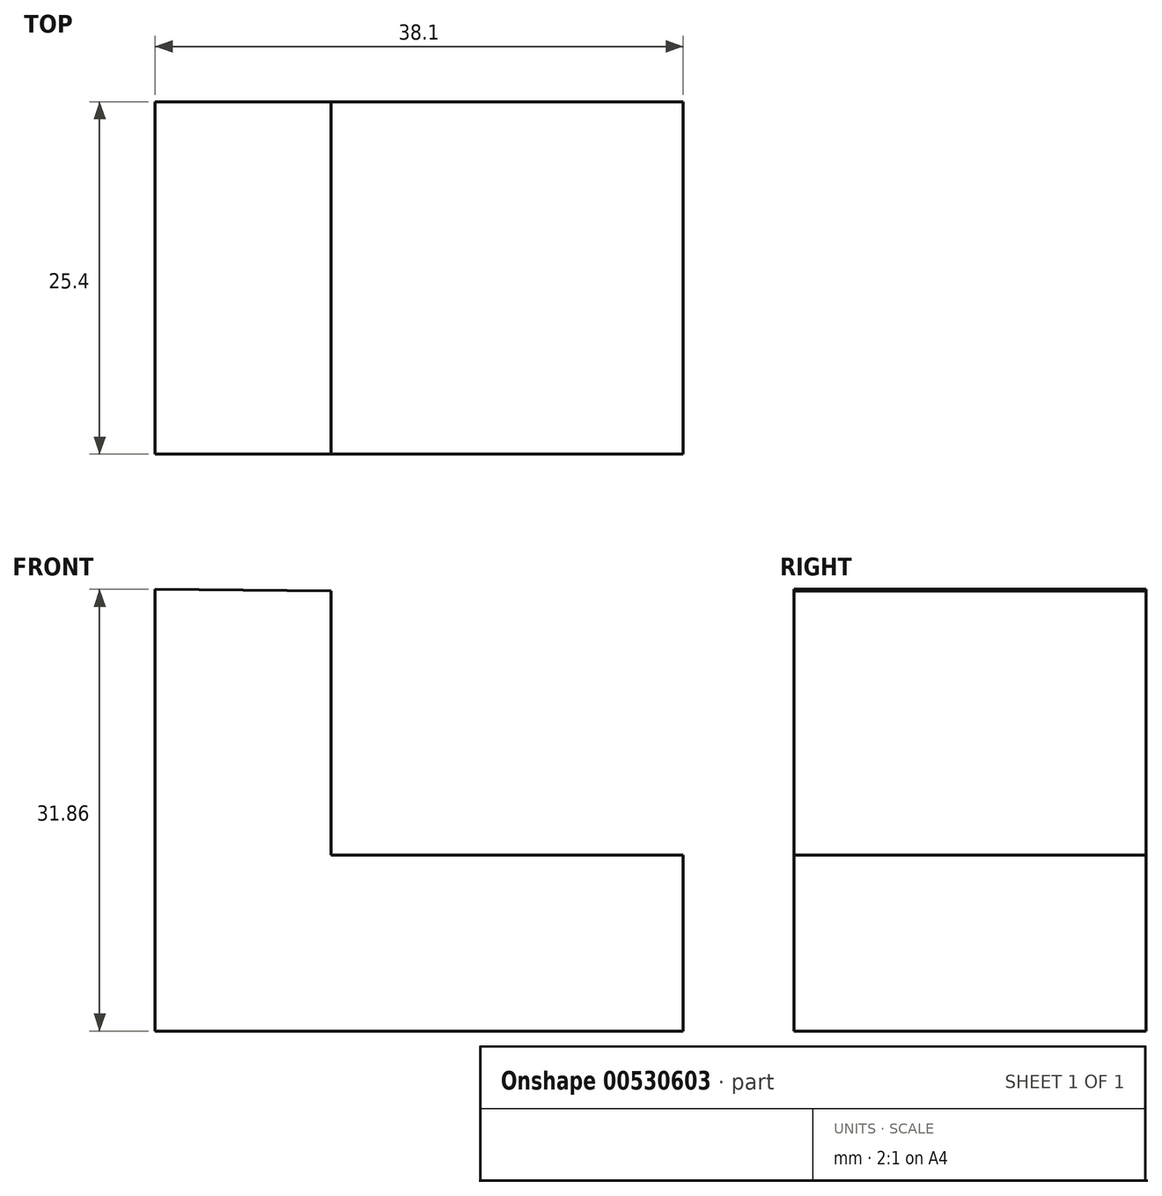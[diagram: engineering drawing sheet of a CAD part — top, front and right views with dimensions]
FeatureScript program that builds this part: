
annotation { "Feature Type Name" : "Feature", "Feature Type Description" : "" }
export const myFeature = defineFeature(function(context is Context, id is Id, definition is map)
    precondition{}
    {
        {
            var Q0;
            Q0=qCreatedBy(makeId("Front.planeOp"),FACE);
            var sketch = newSketch(context, id + "F0", { "sketchPlane" : qUnion([Q0])});
            skLineSegment(sketch, "E0", {"start": v(-47.77, 31.86) * mm, "end": v(-47.77, 0) * mm});
            skLineSegment(sketch, "E1", {"start": v(-47.77, 0) * mm, "end": v(-9.67, 0) * mm});
            skLineSegment(sketch, "E2", {"start": v(-9.67, 0) * mm, "end": v(-9.67, 12.7) * mm});
            skLineSegment(sketch, "E3", {"start": v(-9.67, 12.7) * mm, "end": v(-35.07, 12.7) * mm});
            skLineSegment(sketch, "E4", {"start": v(-35.07, 12.7) * mm, "end": v(-35.07, 31.75) * mm});
            skLineSegment(sketch, "E5", {"start": v(-35.07, 31.75) * mm, "end": v(-47.77, 31.86) * mm});
            skSolve(sketch);
        }
        {
            var Q0;
            Q0 = qSketchRegion(id + "F0", true);
            extrude(context, id + "F1", {"entities" : qUnion([Q0]), "depth" : 25.4 * mm, "offsetDistance" : 25.4 * mm});
        }
    });
